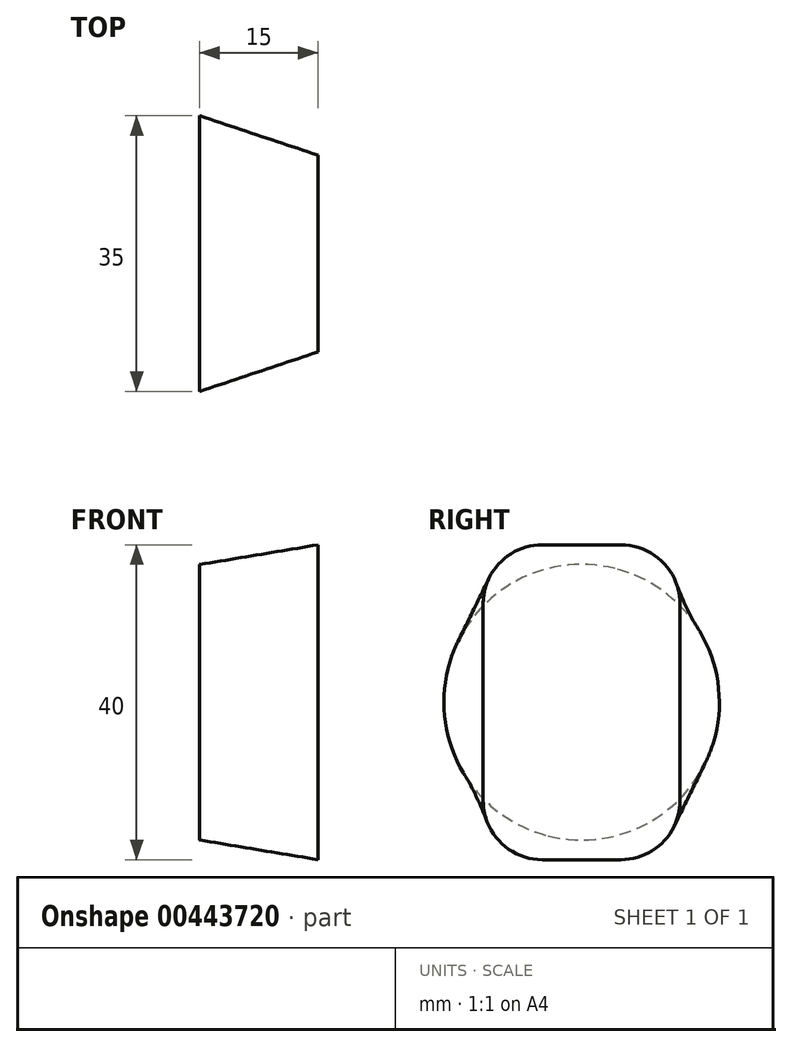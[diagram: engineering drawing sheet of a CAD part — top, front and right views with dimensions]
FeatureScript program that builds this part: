
annotation { "Feature Type Name" : "Feature", "Feature Type Description" : "" }
export const myFeature = defineFeature(function(context is Context, id is Id, definition is map)
    precondition{}
    {
        {
            var Q0;
            Q0=qCreatedBy(makeId("Right.planeOp"),FACE);
            var sketch = newSketch(context, id + "F0", { "sketchPlane" : qUnion([Q0])});
            skCircle(sketch, "E0", {"center": v(0, 0) * mm, "radius": 17.5 * mm});
            skSolve(sketch);
        }
        {
            var Q0;
            Q0=qCreatedBy(makeId("Right.planeOp"),FACE);
            cPlane(context, id + "F1", {"entities" : qUnion([Q0]), "cplaneType" : CPlaneType.OFFSET, "offset" : 15 * mm, "width" : 150 * mm, "height" : 150 * mm});
        }
        {
            var Q0;
            Q0=qCreatedBy(id+"F1.planeOp",FACE);
            var sketch = newSketch(context, id + "F2", { "sketchPlane" : qUnion([Q0])});
            skLineSegment(sketch, "E1.bottom", {"start": v(5, 20) * mm, "end": v(-5, 20) * mm});
            skLineSegment(sketch, "E1.top", {"start": v(5, -20) * mm, "end": v(-5, -20) * mm});
            skLineSegment(sketch, "E1.left", {"start": v(12.5, 12.5) * mm, "end": v(12.5, -12.5) * mm});
            skLineSegment(sketch, "E1.right", {"start": v(-12.5, 12.5) * mm, "end": v(-12.5, -12.5) * mm});
            skPoint(sketch, "E1.middle", {"position": v(0, 0) * mm});
            skPoint(sketch, "E2.visualSharp", {"position": v(-12.5, 20) * mm});
            skArc(sketch, "E2.filletArc", {"start": v(-5, 20) * mm, "mid": v(-10.3, 17.8) * mm, "end": v(-12.5, 12.5) * mm});
            skPoint(sketch, "E3.visualSharp", {"position": v(12.5, 20) * mm});
            skArc(sketch, "E3.filletArc", {"start": v(12.5, 12.5) * mm, "mid": v(10.3, 17.8) * mm, "end": v(5, 20) * mm});
            skPoint(sketch, "E4.visualSharp", {"position": v(12.5, -20) * mm});
            skArc(sketch, "E4.filletArc", {"start": v(5, -20) * mm, "mid": v(10.3, -17.8) * mm, "end": v(12.5, -12.5) * mm});
            skPoint(sketch, "E5.visualSharp", {"position": v(-12.5, -20) * mm});
            skArc(sketch, "E5.filletArc", {"start": v(-12.5, -12.5) * mm, "mid": v(-10.3, -17.8) * mm, "end": v(-5, -20) * mm});
            skSolve(sketch);
        }
        {
            var Q0;
            Q0=makeQuery(id+"F0.imprint","IMPRINT",FACE,{"disambiguationData":[TD([[makeQuery(id+"F0.imprint","IMPRINT",EDGE,{"derivedFrom":sQuery(id+"F0.wireOp",EDGE,"E0")}),1.0]])]});
            var Q1;
            Q1=makeQuery(id+"F2.imprint","IMPRINT",FACE,{"disambiguationData":[TD([[makeQuery(id+"F2.imprint","IMPRINT",EDGE,{"derivedFrom":sQuery(id+"F2.wireOp",EDGE,"E1.bottom")}),1.0]])]});
            loft(context, id + "F3", {"sheetProfilesArray" : [{ "sheetProfileEntities" : qUnion([Q0]) }, { "sheetProfileEntities" : qUnion([Q1]) }]});
        }
    });
